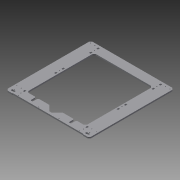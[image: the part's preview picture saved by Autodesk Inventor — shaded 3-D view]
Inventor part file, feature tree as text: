
AUTODESK INVENTOR PART (.ipt)
format: ipt  version: 2015 (Build 190159000, 159)  size: 279,040 bytes
history: native  units: mm
features: extrude x5, sketch x5, hole x1
ambient origin geometry x8: Origin, YZ Plane, XZ Plane, XY Plane, X Axis, Y Axis, Z Axis, Center Point
bodies: Solid1 (feature_tree)
feature tree (11):
  extrude  "Extrusion1"  Depth=25.0mm
  extrude  "Extrusion2"  Depth=4.0mm
  extrude  "Extrusion3"  Depth=4.0mm
  extrude  "Extrusion4"  Depth=7.0mm
  extrude  "Extrusion5"  Depth=2.0mm
  hole  "Hole1"  [1 undecoded]
  sketch  "Sketch1"  dims[d17=0.0mm d30=25.0mm]
  sketch  "Sketch4"  dims[d31=4.0mm d32=4.0mm]
  sketch  "Sketch5"  dims[d33=4.0mm d34=4.0mm]
  sketch  "Sketch7"  dims[d36=7.0mm d37=7.0mm]
  sketch  "Sketch8"  dims[d40=10.0mm d41=0.0mm d42=2.0mm d43=135.0deg d44=20.0mm d45=20.0mm d46=10.0mm d47=0.0mm d48=9.0mm d49=8.75mm d50=6.5mm d51=32.3mm d52=9.257mm d53=32.3mm d54=164.35mm d55=34.65mm d56=10.0mm d57=0.0mm d58=8.0mm d59=8.0mm d60=8.511mm d61=16.026mm d62=10.0mm d63=0.0mm d64=4.0mm d65=4.0mm d66=11.65mm d67=3.25mm d68=20.0mm d69=20.0mm d70=11.65mm d73=9.987mm d74=8.169mm d75=40.0mm d76=20.0mm d77=10.0mm d78=11.64mm d79=90.0mm d81=45.0mm d82=3.6mm d83=6.0mm d84=4.0mm d85=2.0mm d86=90.0deg d87=8.0mm d88=20.594885mm]
note: 1 required parameter value undecoded (feature->parameter linkage not recoverable at this tier; creation-order binding heuristic only, values carry confidence <= 0.55)
